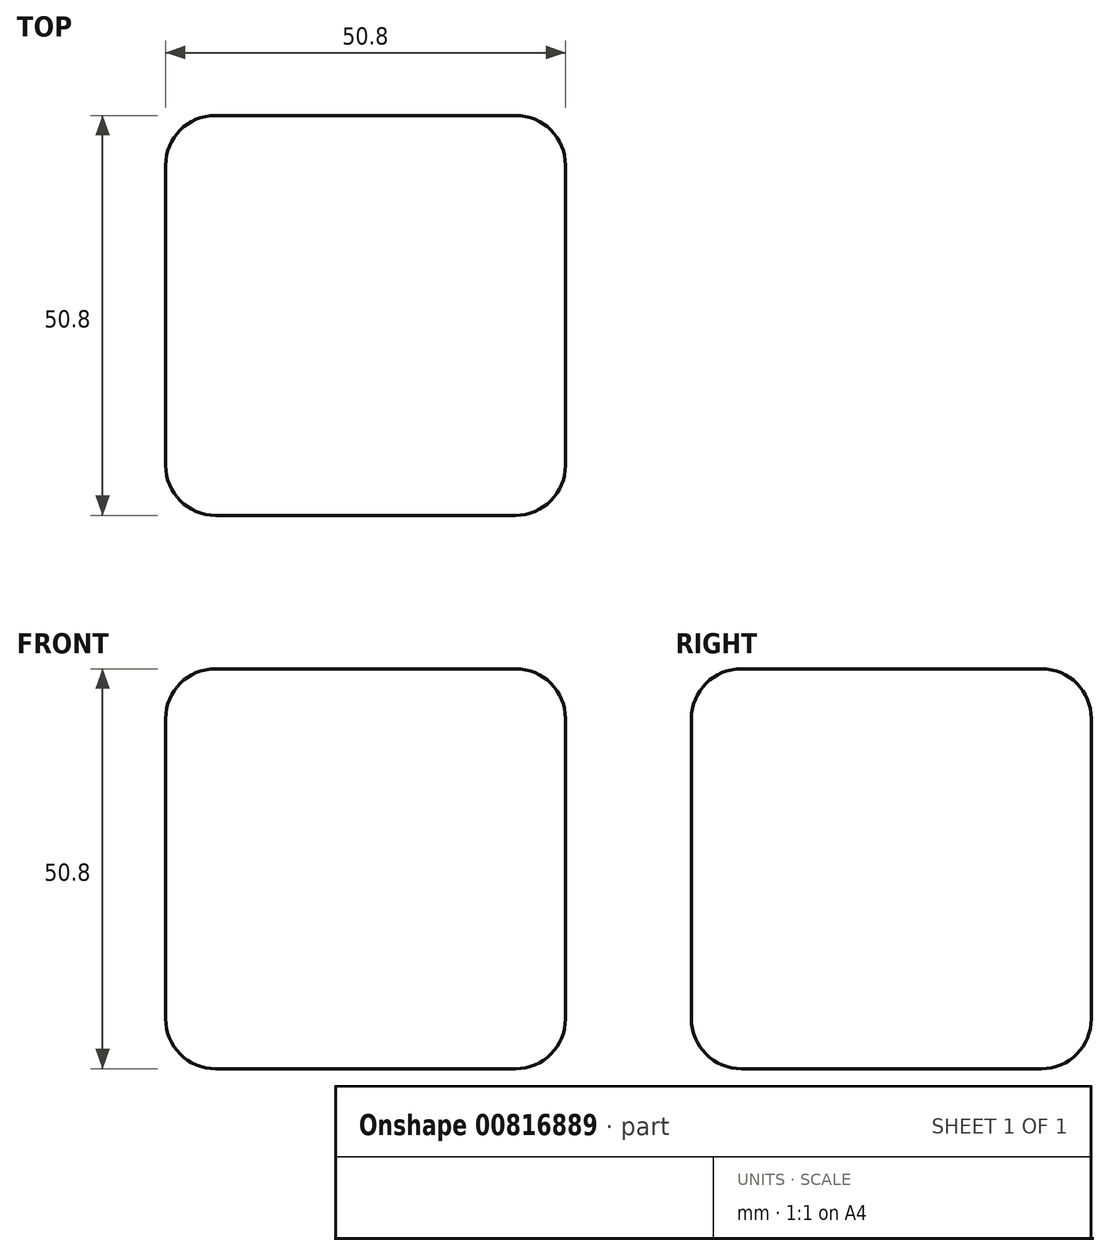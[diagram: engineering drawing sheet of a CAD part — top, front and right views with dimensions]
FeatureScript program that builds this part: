
annotation { "Feature Type Name" : "Feature", "Feature Type Description" : "" }
export const myFeature = defineFeature(function(context is Context, id is Id, definition is map)
    precondition{}
    {
        {
            var Q0;
            Q0=qCreatedBy(makeId("Top.planeOp"),FACE);
            var sketch = newSketch(context, id + "F0", { "sketchPlane" : qUnion([Q0])});
            skLineSegment(sketch, "E0.bottom", {"start": v(0, 18.6) * mm, "end": v(-50.8, 18.6) * mm});
            skLineSegment(sketch, "E0.top", {"start": v(0, 69.4) * mm, "end": v(-50.8, 69.4) * mm});
            skLineSegment(sketch, "E0.left", {"start": v(0, 18.6) * mm, "end": v(0, 69.4) * mm});
            skLineSegment(sketch, "E0.right", {"start": v(-50.8, 18.6) * mm, "end": v(-50.8, 69.4) * mm});
            skPoint(sketch, "E0.middle", {"position": v(-25.4, 44) * mm});
            skSolve(sketch);
        }
        {
            var Q0;
            Q0=makeQuery(id+"F0.imprint","IMPRINT",FACE,{"disambiguationData":[TD([[makeQuery(id+"F0.imprint","IMPRINT",EDGE,{"derivedFrom":sQuery(id+"F0.wireOp",EDGE,"E0.bottom")}),-1.0]])]});
            extrude(context, id + "F1", {"entities" : qUnion([Q0]), "depth" : 50.8 * mm, "offsetDistance" : 25.4 * mm});
        }
        {
            var Q0;
            Q0=makeQuery(id+"F1.opExtrude","SWEPT_EDGE",EDGE,{"disambiguationData":[OSD([sQuery(id+"F0.wireOp",EDGE,"E0.bottom"),sQuery(id+"F0.wireOp",EDGE,"E0.left")])]});
            var Q1;
            Q1=makeQuery(id+"F1.opExtrude","SWEPT_EDGE",EDGE,{"disambiguationData":[OSD([sQuery(id+"F0.wireOp",EDGE,"E0.bottom"),sQuery(id+"F0.wireOp",EDGE,"E0.right")])]});
            var Q2;
            Q2=makeQuery(id+"F1.opExtrude","CAP_EDGE",EDGE,{"disambiguationData":[OSD([sQuery(id+"F0.wireOp",EDGE,"E0.bottom")])],"isStart":true});
            var Q3;
            Q3=makeQuery(id+"F1.opExtrude","CAP_EDGE",EDGE,{"disambiguationData":[OSD([sQuery(id+"F0.wireOp",EDGE,"E0.bottom")])],"isStart":false});
            var Q4;
            Q4=makeQuery(id+"F1.opExtrude","CAP_EDGE",EDGE,{"disambiguationData":[OSD([sQuery(id+"F0.wireOp",EDGE,"E0.top")])],"isStart":false});
            var Q5;
            Q5=makeQuery(id+"F1.opExtrude","SWEPT_EDGE",EDGE,{"disambiguationData":[OSD([sQuery(id+"F0.wireOp",EDGE,"E0.top"),sQuery(id+"F0.wireOp",EDGE,"E0.left")])]});
            var Q6;
            Q6=makeQuery(id+"F1.opExtrude","SWEPT_EDGE",EDGE,{"disambiguationData":[OSD([sQuery(id+"F0.wireOp",EDGE,"E0.top"),sQuery(id+"F0.wireOp",EDGE,"E0.right")])]});
            var Q7;
            Q7=makeQuery(id+"F1.opExtrude","CAP_EDGE",EDGE,{"disambiguationData":[OSD([sQuery(id+"F0.wireOp",EDGE,"E0.top")])],"isStart":true});
            var Q8;
            Q8=makeQuery(id+"F1.opExtrude","CAP_EDGE",EDGE,{"disambiguationData":[OSD([sQuery(id+"F0.wireOp",EDGE,"E0.left")])],"isStart":true});
            var Q9;
            Q9=makeQuery(id+"F1.opExtrude","CAP_EDGE",EDGE,{"disambiguationData":[OSD([sQuery(id+"F0.wireOp",EDGE,"E0.left")])],"isStart":false});
            var Q10;
            Q10=makeQuery(id+"F1.opExtrude","CAP_EDGE",EDGE,{"disambiguationData":[OSD([sQuery(id+"F0.wireOp",EDGE,"E0.right")])],"isStart":true});
            var Q11;
            Q11=makeQuery(id+"F1.opExtrude","CAP_EDGE",EDGE,{"disambiguationData":[OSD([sQuery(id+"F0.wireOp",EDGE,"E0.right")])],"isStart":false});
            fillet(context, id + "F2", {"entities" : qUnion([Q0, Q1, Q2, Q3, Q4, Q5, Q6, Q7, Q8, Q9, Q10, Q11]), "radius" : 6.35 * mm, "tangentPropagation" : true, "allowEdgeOverflow" : false});
        }
    });
